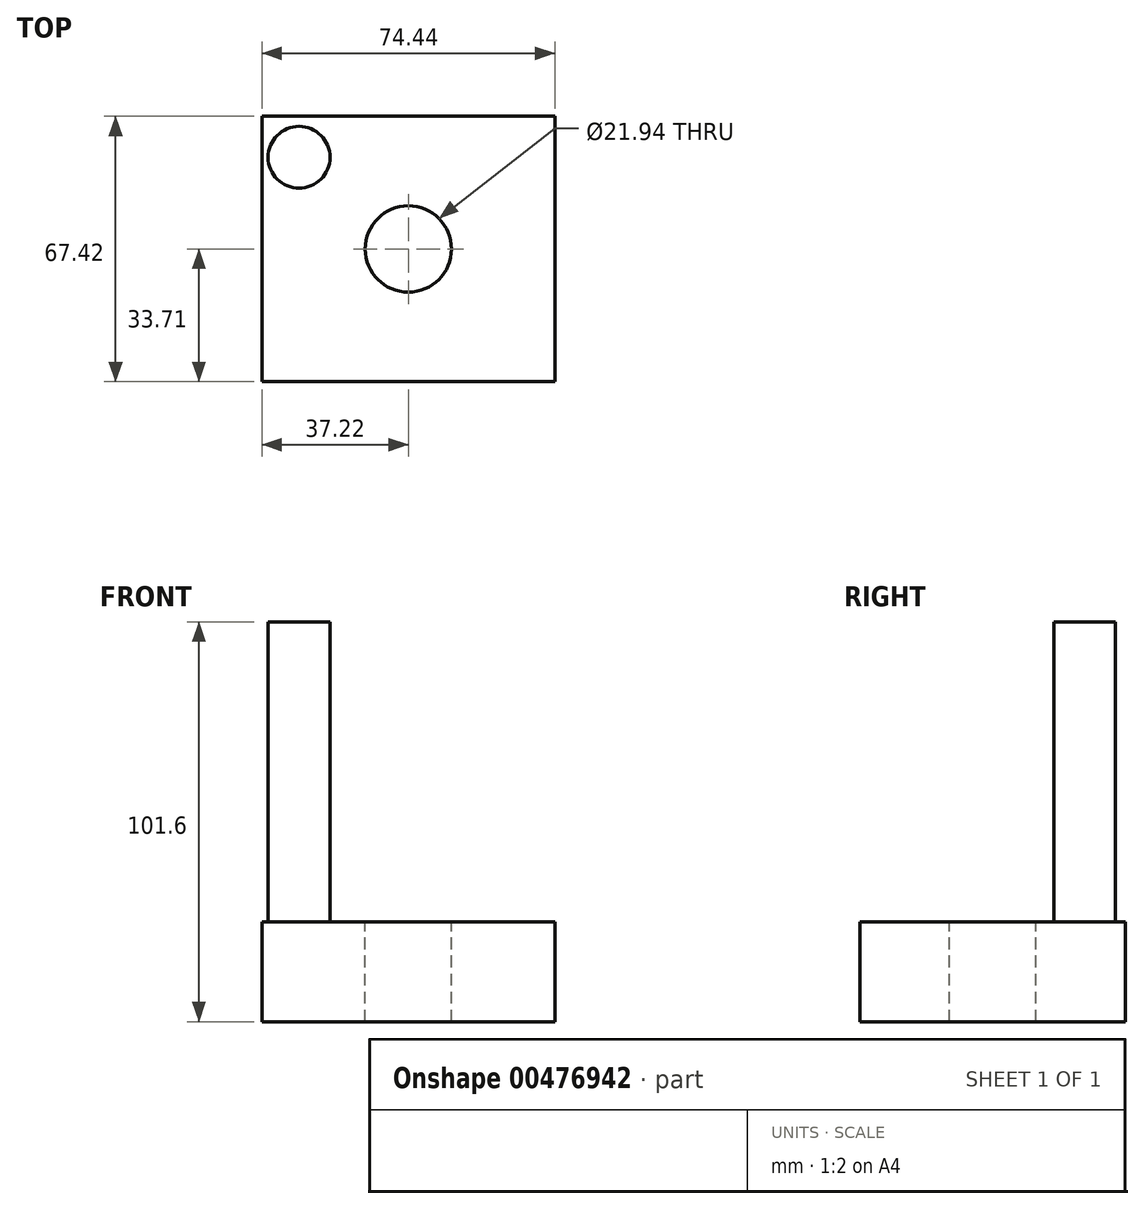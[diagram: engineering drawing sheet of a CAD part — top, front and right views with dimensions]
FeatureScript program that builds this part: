
annotation { "Feature Type Name" : "Feature", "Feature Type Description" : "" }
export const myFeature = defineFeature(function(context is Context, id is Id, definition is map)
    precondition{}
    {
        {
            var Q0;
            Q0=qCreatedBy(makeId("Top.planeOp"),FACE);
            var sketch = newSketch(context, id + "F0", { "sketchPlane" : qUnion([Q0])});
            skLineSegment(sketch, "E0.bottom", {"start": v(37.22, -33.7) * mm, "end": v(-37.22, -33.7) * mm});
            skLineSegment(sketch, "E0.top", {"start": v(37.22, 33.7) * mm, "end": v(-37.22, 33.7) * mm});
            skLineSegment(sketch, "E0.left", {"start": v(37.22, -33.7) * mm, "end": v(37.22, 33.7) * mm});
            skLineSegment(sketch, "E0.right", {"start": v(-37.22, -33.7) * mm, "end": v(-37.22, 33.7) * mm});
            skPoint(sketch, "E0.middle", {"position": v(0, 0) * mm});
            skSolve(sketch);
        }
        {
            var Q0;
            Q0 = qSketchRegion(id + "F0", true);
            extrude(context, id + "F1", {"entities" : qUnion([Q0]), "depth" : 25.4 * mm});
        }
        {
            var Q0;
            Q0=makeQuery(id+"F1.opExtrude","CAP_FACE",FACE,{"disambiguationData":[OSD([sQuery(id+"F0.wireOp",EDGE,"E0.bottom"),sQuery(id+"F0.wireOp",EDGE,"E0.top"),sQuery(id+"F0.wireOp",EDGE,"E0.left"),sQuery(id+"F0.wireOp",EDGE,"E0.right")])],"isStart":false});
            var sketch = newSketch(context, id + "F2", { "sketchPlane" : qUnion([Q0])});
            skCircle(sketch, "E1", {"center": v(0, 0) * mm, "radius": 10.97 * mm});
            skSolve(sketch);
        }
        {
            var Q0;
            Q0 = qSketchRegion(id + "F2", true);
            extrude(context, id + "F3", {"entities" : qUnion([Q0]), "operationType" : NewBodyOperationType.REMOVE, "endBound" : BoundingType.THROUGH_ALL, "oppositeDirection" : true, "depth" : 25.4 * mm});
        }
        {
            var Q0;
            Q0=makeQuery(id+"F1.opExtrude","CAP_FACE",FACE,{"disambiguationData":[OSD([sQuery(id+"F0.wireOp",EDGE,"E0.bottom"),sQuery(id+"F0.wireOp",EDGE,"E0.top"),sQuery(id+"F0.wireOp",EDGE,"E0.left"),sQuery(id+"F0.wireOp",EDGE,"E0.right")])],"isStart":false});
            var sketch = newSketch(context, id + "F4", { "sketchPlane" : qUnion([Q0])});
            skCircle(sketch, "E2", {"center": v(-27.76, 23.32) * mm, "radius": 7.85 * mm});
            skSolve(sketch);
        }
        {
            var Q0;
            Q0 = qSketchRegion(id + "F4", true);
            extrude(context, id + "F5", {"entities" : qUnion([Q0]), "operationType" : NewBodyOperationType.ADD, "depth" : 76.2 * mm});
        }
    });
